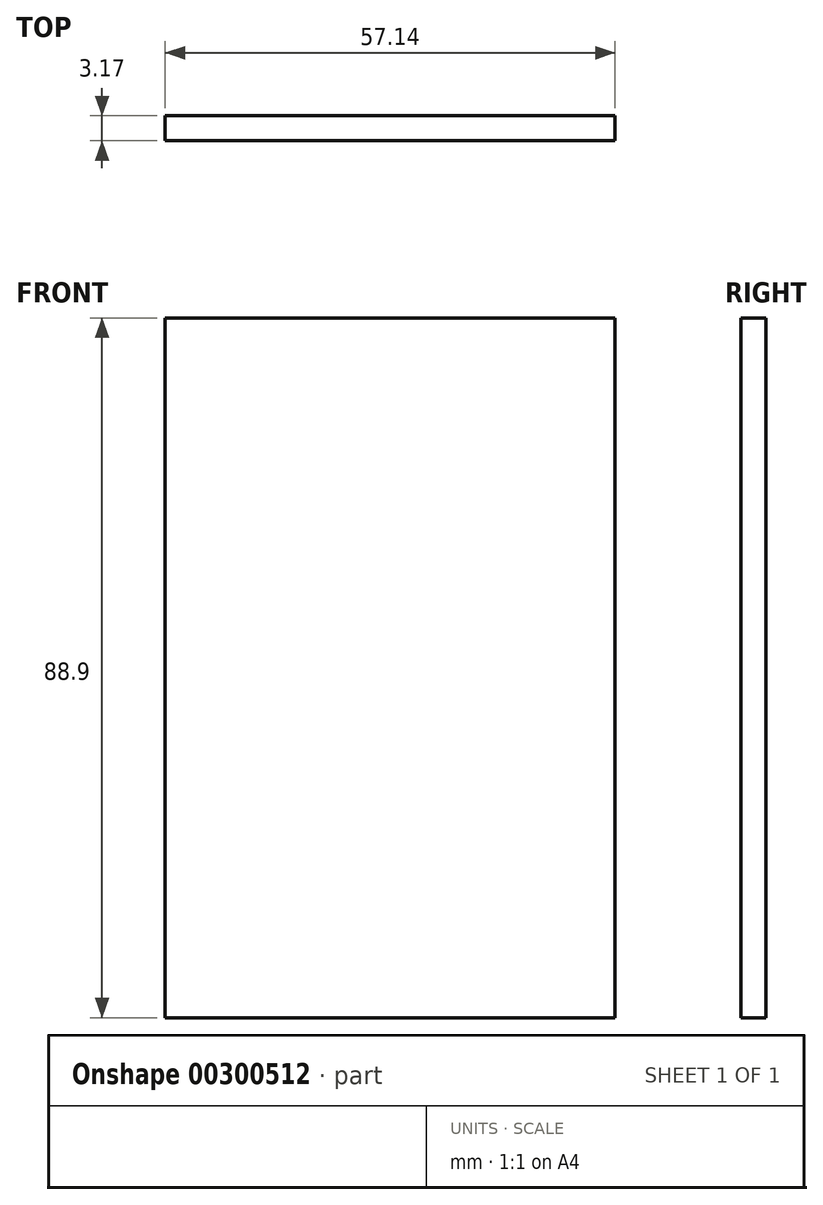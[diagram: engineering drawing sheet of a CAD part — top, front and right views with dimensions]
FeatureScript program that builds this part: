
annotation { "Feature Type Name" : "Feature", "Feature Type Description" : "" }
export const myFeature = defineFeature(function(context is Context, id is Id, definition is map)
    precondition{}
    {
        {
            var Q0;
            Q0=qCreatedBy(makeId("Front.planeOp"),FACE);
            var sketch = newSketch(context, id + "F0", { "sketchPlane" : qUnion([Q0])});
            skLineSegment(sketch, "E0.bottom", {"start": v(-28.57, -44.45) * mm, "end": v(28.58, -44.45) * mm});
            skLineSegment(sketch, "E0.top", {"start": v(-28.58, 44.45) * mm, "end": v(28.57, 44.45) * mm});
            skLineSegment(sketch, "E0.left", {"start": v(-28.57, -44.45) * mm, "end": v(-28.58, 44.45) * mm});
            skLineSegment(sketch, "E0.right", {"start": v(28.58, -44.45) * mm, "end": v(28.57, 44.45) * mm});
            skPoint(sketch, "E0.middle", {"position": v(0, 0) * mm});
            skSolve(sketch);
        }
        {
            var Q0;
            Q0 = qSketchRegion(id + "F0", true);
            extrude(context, id + "F1", {"entities" : qUnion([Q0]), "depth" : 3.17 * mm});
        }
    });
